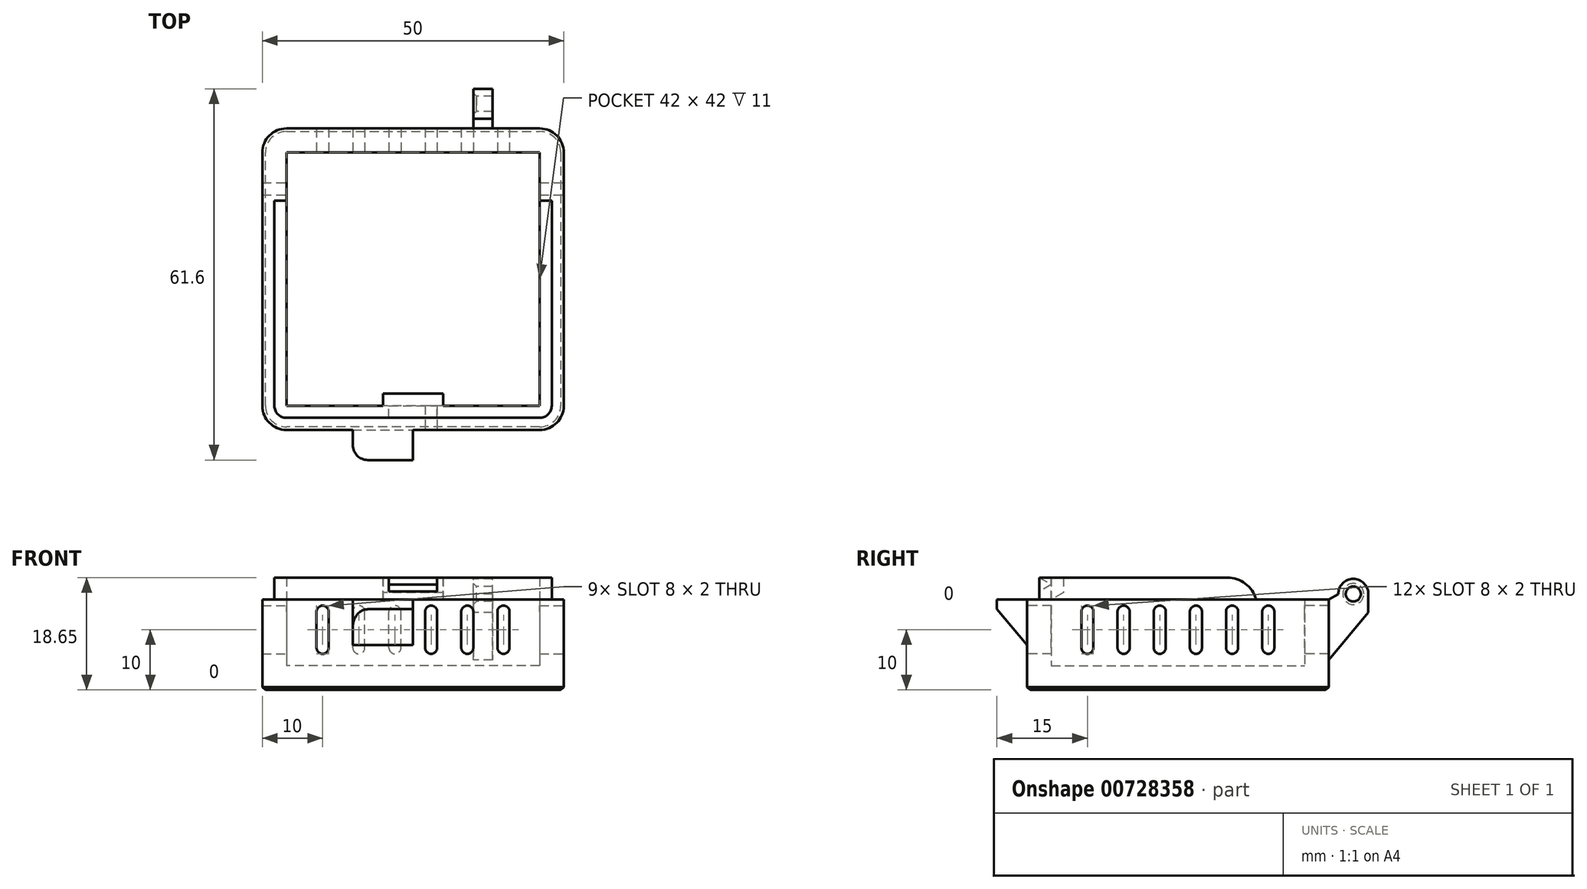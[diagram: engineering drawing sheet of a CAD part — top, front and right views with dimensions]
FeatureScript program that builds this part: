
annotation { "Feature Type Name" : "Feature", "Feature Type Description" : "" }
export const myFeature = defineFeature(function(context is Context, id is Id, definition is map)
    precondition{}
    {
        {
            var Q0;
            Q0=qCreatedBy(makeId("Top.planeOp"),FACE);
            var sketch = newSketch(context, id + "F0", { "sketchPlane" : qUnion([Q0])});
            skLineSegment(sketch, "E0.bottom", {"start": v(25, -25) * mm, "end": v(-25, -25) * mm});
            skLineSegment(sketch, "E0.top", {"start": v(25, 25) * mm, "end": v(-25, 25) * mm});
            skLineSegment(sketch, "E0.left", {"start": v(25, -25) * mm, "end": v(25, 25) * mm});
            skLineSegment(sketch, "E0.right", {"start": v(-25, -25) * mm, "end": v(-25, 25) * mm});
            skPoint(sketch, "E0.middle", {"position": v(0, 0) * mm});
            skSolve(sketch);
        }
        {
            var Q0;
            Q0=qSketchRegion(id+"F0",true);
            extrude(context, id + "F1", {"entities" : qUnion([Q0]), "depth" : 20 * mm, "offsetDistance" : 25 * mm});
        }
        {
            var Q0;
            Q0=makeQuery(id+"F1.opExtrude","CAP_FACE",FACE,{"disambiguationData":[OSD([sQuery(id+"F0.wireOp",EDGE,"E0.bottom"),sQuery(id+"F0.wireOp",EDGE,"E0.top"),sQuery(id+"F0.wireOp",EDGE,"E0.left"),sQuery(id+"F0.wireOp",EDGE,"E0.right")])],"isStart":false});
            shell(context, id + "F2", {"entities" : qUnion([Q0]), "thickness" : 4 * mm});
        }
        {
            var Q0;
            Q0=makeQuery(id+"F1.opExtrude","SWEPT_EDGE",EDGE,{"disambiguationData":[OSD([sQuery(id+"F0.wireOp",EDGE,"E0.bottom"),sQuery(id+"F0.wireOp",EDGE,"E0.right")])]});
            var Q1;
            Q1=makeQuery(id+"F1.opExtrude","SWEPT_EDGE",EDGE,{"disambiguationData":[OSD([sQuery(id+"F0.wireOp",EDGE,"E0.bottom"),sQuery(id+"F0.wireOp",EDGE,"E0.left")])]});
            var Q2;
            Q2=makeQuery(id+"F1.opExtrude","SWEPT_EDGE",EDGE,{"disambiguationData":[OSD([sQuery(id+"F0.wireOp",EDGE,"E0.top"),sQuery(id+"F0.wireOp",EDGE,"E0.left")])]});
            var Q3;
            Q3=makeQuery(id+"F1.opExtrude","SWEPT_EDGE",EDGE,{"disambiguationData":[OSD([sQuery(id+"F0.wireOp",EDGE,"E0.top"),sQuery(id+"F0.wireOp",EDGE,"E0.right")])]});
            fillet(context, id + "F3", {"entities" : qUnion([Q0, Q1, Q2, Q3]), "radius" : 4 * mm, "tangentPropagation" : true, "allowEdgeOverflow" : false});
        }
        {
            var Q0;
            Q0=makeQuery(id+"F1.opExtrude","SWEPT_FACE",FACE,{"disambiguationData":[OSD([sQuery(id+"F0.wireOp",EDGE,"E0.bottom")])]});
            var sketch = newSketch(context, id + "F4", { "sketchPlane" : qUnion([Q0])});
            skLineSegment(sketch, "E1.bottom", {"start": v(-15, 6) * mm, "end": v(-15, 6) * mm});
            skLineSegment(sketch, "E1.top", {"start": v(-15, 14) * mm, "end": v(-15, 14) * mm});
            skLineSegment(sketch, "E1.left", {"start": v(-14, 7) * mm, "end": v(-14, 13) * mm});
            skLineSegment(sketch, "E1.right", {"start": v(-16, 7) * mm, "end": v(-16, 13) * mm});
            skPoint(sketch, "E1.middle", {"position": v(-15, 10) * mm});
            skLineSegment(sketch, "E2.1.0.0", {"start": v(-9, 14) * mm, "end": v(-9, 14) * mm});
            skLineSegment(sketch, "E2.1.0.1", {"start": v(-10, 7) * mm, "end": v(-10, 13) * mm});
            skLineSegment(sketch, "E2.1.0.2", {"start": v(-9, 6) * mm, "end": v(-9, 6) * mm});
            skLineSegment(sketch, "E2.1.0.3", {"start": v(-8, 7) * mm, "end": v(-8, 13) * mm});
            skPoint(sketch, "E2.1.0.4", {"position": v(-9, 10) * mm});
            skLineSegment(sketch, "E2.2.0.0", {"start": v(-3, 14) * mm, "end": v(-3, 14) * mm});
            skLineSegment(sketch, "E2.2.0.1", {"start": v(-4, 7) * mm, "end": v(-4, 13) * mm});
            skLineSegment(sketch, "E2.2.0.2", {"start": v(-3, 6) * mm, "end": v(-3, 6) * mm});
            skLineSegment(sketch, "E2.2.0.3", {"start": v(-2, 7) * mm, "end": v(-2, 13) * mm});
            skPoint(sketch, "E2.2.0.4", {"position": v(-3, 10) * mm});
            skLineSegment(sketch, "E2.3.0.0", {"start": v(3, 14) * mm, "end": v(3, 14) * mm});
            skLineSegment(sketch, "E2.3.0.1", {"start": v(2, 7) * mm, "end": v(2, 13) * mm});
            skLineSegment(sketch, "E2.3.0.2", {"start": v(3, 6) * mm, "end": v(3, 6) * mm});
            skLineSegment(sketch, "E2.3.0.3", {"start": v(4, 7) * mm, "end": v(4, 13) * mm});
            skPoint(sketch, "E2.3.0.4", {"position": v(3, 10) * mm});
            skLineSegment(sketch, "E2.4.0.0", {"start": v(9, 14) * mm, "end": v(9, 14) * mm});
            skLineSegment(sketch, "E2.4.0.1", {"start": v(8, 7) * mm, "end": v(8, 13) * mm});
            skLineSegment(sketch, "E2.4.0.2", {"start": v(9, 6) * mm, "end": v(9, 6) * mm});
            skLineSegment(sketch, "E2.4.0.3", {"start": v(10, 7) * mm, "end": v(10, 13) * mm});
            skPoint(sketch, "E2.4.0.4", {"position": v(9, 10) * mm});
            skLineSegment(sketch, "E2.direction1", {"start": v(-16, 6) * mm, "end": v(-10, 6) * mm, "construction": true});
            skLineSegment(sketch, "E3.MirrorCS", {"start": v(15, 6) * mm, "end": v(15, 6) * mm});
            skLineSegment(sketch, "E4.MirrorCS", {"start": v(16, 7) * mm, "end": v(16, 13) * mm});
            skLineSegment(sketch, "E5.MirrorCS", {"start": v(14, 7) * mm, "end": v(14, 13) * mm});
            skLineSegment(sketch, "E6.MirrorCS", {"start": v(15, 14) * mm, "end": v(15, 14) * mm});
            skPoint(sketch, "E7.MirrorP", {"position": v(15, 10) * mm});
            skLineSegment(sketch, "E8.MirrorCS", {"start": v(16, 6) * mm, "end": v(10, 6) * mm, "construction": true});
            skPoint(sketch, "E9.visualSharp", {"position": v(-16, 14) * mm});
            skArc(sketch, "E9.filletArc", {"start": v(-15, 14) * mm, "mid": v(-15.7, 13.7) * mm, "end": v(-16, 13) * mm});
            skPoint(sketch, "E10.visualSharp", {"position": v(-14, 14) * mm});
            skArc(sketch, "E10.filletArc", {"start": v(-14, 13) * mm, "mid": v(-14.3, 13.7) * mm, "end": v(-15, 14) * mm});
            skPoint(sketch, "E11.visualSharp", {"position": v(-16, 6) * mm});
            skArc(sketch, "E11.filletArc", {"start": v(-16, 7) * mm, "mid": v(-15.7, 6.3) * mm, "end": v(-15, 6) * mm});
            skPoint(sketch, "E12.visualSharp", {"position": v(-14, 6) * mm});
            skArc(sketch, "E12.filletArc", {"start": v(-15, 6) * mm, "mid": v(-14.3, 6.3) * mm, "end": v(-14, 7) * mm});
            skPoint(sketch, "E13.visualSharp", {"position": v(-10, 14) * mm});
            skArc(sketch, "E13.filletArc", {"start": v(-9, 14) * mm, "mid": v(-9.7, 13.7) * mm, "end": v(-10, 13) * mm});
            skPoint(sketch, "E14.visualSharp", {"position": v(-8, 14) * mm});
            skArc(sketch, "E14.filletArc", {"start": v(-8, 13) * mm, "mid": v(-8.3, 13.7) * mm, "end": v(-9, 14) * mm});
            skPoint(sketch, "E15.visualSharp", {"position": v(-8, 6) * mm});
            skArc(sketch, "E15.filletArc", {"start": v(-9, 6) * mm, "mid": v(-8.3, 6.3) * mm, "end": v(-8, 7) * mm});
            skPoint(sketch, "E16.visualSharp", {"position": v(-10, 6) * mm});
            skArc(sketch, "E16.filletArc", {"start": v(-10, 7) * mm, "mid": v(-9.7, 6.3) * mm, "end": v(-9, 6) * mm});
            skPoint(sketch, "E17.visualSharp", {"position": v(-4, 6) * mm});
            skArc(sketch, "E17.filletArc", {"start": v(-4, 7) * mm, "mid": v(-3.7, 6.3) * mm, "end": v(-3, 6) * mm});
            skPoint(sketch, "E18.visualSharp", {"position": v(-2, 6) * mm});
            skArc(sketch, "E18.filletArc", {"start": v(-3, 6) * mm, "mid": v(-2.3, 6.3) * mm, "end": v(-2, 7) * mm});
            skPoint(sketch, "E19.visualSharp", {"position": v(-2, 14) * mm});
            skArc(sketch, "E19.filletArc", {"start": v(-2, 13) * mm, "mid": v(-2.3, 13.7) * mm, "end": v(-3, 14) * mm});
            skPoint(sketch, "E20.visualSharp", {"position": v(-4, 14) * mm});
            skArc(sketch, "E20.filletArc", {"start": v(-3, 14) * mm, "mid": v(-3.7, 13.7) * mm, "end": v(-4, 13) * mm});
            skPoint(sketch, "E21.visualSharp", {"position": v(2, 14) * mm});
            skArc(sketch, "E21.filletArc", {"start": v(3, 14) * mm, "mid": v(2.3, 13.7) * mm, "end": v(2, 13) * mm});
            skPoint(sketch, "E22.visualSharp", {"position": v(4, 14) * mm});
            skArc(sketch, "E22.filletArc", {"start": v(4, 13) * mm, "mid": v(3.7, 13.7) * mm, "end": v(3, 14) * mm});
            skPoint(sketch, "E23.visualSharp", {"position": v(4, 6) * mm});
            skArc(sketch, "E23.filletArc", {"start": v(3, 6) * mm, "mid": v(3.7, 6.3) * mm, "end": v(4, 7) * mm});
            skPoint(sketch, "E24.visualSharp", {"position": v(2, 6) * mm});
            skArc(sketch, "E24.filletArc", {"start": v(2, 7) * mm, "mid": v(2.3, 6.3) * mm, "end": v(3, 6) * mm});
            skPoint(sketch, "E25.visualSharp", {"position": v(10, 14) * mm});
            skArc(sketch, "E25.filletArc", {"start": v(10, 13) * mm, "mid": v(9.7, 13.7) * mm, "end": v(9, 14) * mm});
            skPoint(sketch, "E26.visualSharp", {"position": v(8, 14) * mm});
            skArc(sketch, "E26.filletArc", {"start": v(9, 14) * mm, "mid": v(8.3, 13.7) * mm, "end": v(8, 13) * mm});
            skPoint(sketch, "E27.visualSharp", {"position": v(8, 6) * mm});
            skArc(sketch, "E27.filletArc", {"start": v(8, 7) * mm, "mid": v(8.3, 6.3) * mm, "end": v(9, 6) * mm});
            skPoint(sketch, "E28.visualSharp", {"position": v(10, 6) * mm});
            skArc(sketch, "E28.filletArc", {"start": v(9, 6) * mm, "mid": v(9.7, 6.3) * mm, "end": v(10, 7) * mm});
            skPoint(sketch, "E29.visualSharp", {"position": v(16, 14) * mm});
            skArc(sketch, "E29.filletArc", {"start": v(16, 13) * mm, "mid": v(15.7, 13.7) * mm, "end": v(15, 14) * mm});
            skPoint(sketch, "E30.visualSharp", {"position": v(14, 14) * mm});
            skArc(sketch, "E30.filletArc", {"start": v(15, 14) * mm, "mid": v(14.3, 13.7) * mm, "end": v(14, 13) * mm});
            skPoint(sketch, "E31.visualSharp", {"position": v(16, 6) * mm});
            skArc(sketch, "E31.filletArc", {"start": v(15, 6) * mm, "mid": v(15.7, 6.3) * mm, "end": v(16, 7) * mm});
            skPoint(sketch, "E32.visualSharp", {"position": v(14, 6) * mm});
            skArc(sketch, "E32.filletArc", {"start": v(14, 7) * mm, "mid": v(14.3, 6.3) * mm, "end": v(15, 6) * mm});
            skSolve(sketch);
        }
        {
            var Q0;
            Q0=qSketchRegion(id+"F4",true);
            extrude(context, id + "F5", {"entities" : qUnion([Q0]), "operationType" : NewBodyOperationType.REMOVE, "oppositeDirection" : true, "depth" : 50 * mm, "offsetDistance" : 25 * mm});
        }
        {
            var Q0;
            Q0=makeQuery(id+"F1.opExtrude","SWEPT_FACE",FACE,{"disambiguationData":[OSD([sQuery(id+"F0.wireOp",EDGE,"E0.left")])]});
            var sketch = newSketch(context, id + "F6", { "sketchPlane" : qUnion([Q0])});
            skLineSegment(sketch, "E33.bottom", {"start": v(-15, 6) * mm, "end": v(-15, 6) * mm});
            skLineSegment(sketch, "E33.top", {"start": v(-15, 14) * mm, "end": v(-15, 14) * mm});
            skLineSegment(sketch, "E33.left", {"start": v(-14, 7) * mm, "end": v(-14, 13) * mm});
            skLineSegment(sketch, "E33.right", {"start": v(-16, 7) * mm, "end": v(-16, 13) * mm});
            skPoint(sketch, "E33.middle", {"position": v(-15, 10) * mm});
            skPoint(sketch, "E34.visualSharp", {"position": v(-16, 14) * mm});
            skArc(sketch, "E34.filletArc", {"start": v(-15, 14) * mm, "mid": v(-15.7, 13.7) * mm, "end": v(-16, 13) * mm});
            skPoint(sketch, "E35.visualSharp", {"position": v(-14, 14) * mm});
            skArc(sketch, "E35.filletArc", {"start": v(-14, 13) * mm, "mid": v(-14.3, 13.7) * mm, "end": v(-15, 14) * mm});
            skPoint(sketch, "E36.visualSharp", {"position": v(-14, 6) * mm});
            skArc(sketch, "E36.filletArc", {"start": v(-15, 6) * mm, "mid": v(-14.3, 6.3) * mm, "end": v(-14, 7) * mm});
            skPoint(sketch, "E37.visualSharp", {"position": v(-16, 6) * mm});
            skArc(sketch, "E37.filletArc", {"start": v(-16, 7) * mm, "mid": v(-15.7, 6.3) * mm, "end": v(-15, 6) * mm});
            skPoint(sketch, "E38.1.0.0", {"position": v(-8, 6) * mm});
            skPoint(sketch, "E38.1.0.1", {"position": v(-10, 6) * mm});
            skLineSegment(sketch, "E38.1.0.2", {"start": v(-10, 7) * mm, "end": v(-10, 13) * mm});
            skLineSegment(sketch, "E38.1.0.3", {"start": v(-8, 7) * mm, "end": v(-8, 13) * mm});
            skPoint(sketch, "E38.1.0.4", {"position": v(-8, 14) * mm});
            skPoint(sketch, "E38.1.0.5", {"position": v(-10, 14) * mm});
            skPoint(sketch, "E38.1.0.6", {"position": v(-9, 10) * mm});
            skArc(sketch, "E38.1.0.7", {"start": v(-9, 6) * mm, "mid": v(-8.3, 6.3) * mm, "end": v(-8, 7) * mm});
            skArc(sketch, "E38.1.0.8", {"start": v(-8, 13) * mm, "mid": v(-8.3, 13.7) * mm, "end": v(-9, 14) * mm});
            skArc(sketch, "E38.1.0.9", {"start": v(-9, 14) * mm, "mid": v(-9.7, 13.7) * mm, "end": v(-10, 13) * mm});
            skArc(sketch, "E38.1.0.10", {"start": v(-10, 7) * mm, "mid": v(-9.7, 6.3) * mm, "end": v(-9, 6) * mm});
            skPoint(sketch, "E38.2.0.0", {"position": v(-2, 6) * mm});
            skPoint(sketch, "E38.2.0.1", {"position": v(-4, 6) * mm});
            skLineSegment(sketch, "E38.2.0.2", {"start": v(-4, 7) * mm, "end": v(-4, 13) * mm});
            skLineSegment(sketch, "E38.2.0.3", {"start": v(-2, 7) * mm, "end": v(-2, 13) * mm});
            skPoint(sketch, "E38.2.0.4", {"position": v(-2, 14) * mm});
            skPoint(sketch, "E38.2.0.5", {"position": v(-4, 14) * mm});
            skPoint(sketch, "E38.2.0.6", {"position": v(-3, 10) * mm});
            skArc(sketch, "E38.2.0.7", {"start": v(-3, 6) * mm, "mid": v(-2.3, 6.3) * mm, "end": v(-2, 7) * mm});
            skArc(sketch, "E38.2.0.8", {"start": v(-2, 13) * mm, "mid": v(-2.3, 13.7) * mm, "end": v(-3, 14) * mm});
            skArc(sketch, "E38.2.0.9", {"start": v(-3, 14) * mm, "mid": v(-3.7, 13.7) * mm, "end": v(-4, 13) * mm});
            skArc(sketch, "E38.2.0.10", {"start": v(-4, 7) * mm, "mid": v(-3.7, 6.3) * mm, "end": v(-3, 6) * mm});
            skLineSegment(sketch, "E38.direction1", {"start": v(-16, 6) * mm, "end": v(-10, 6) * mm, "construction": true});
            skArc(sketch, "E39.MirrorCS", {"start": v(10, 7) * mm, "mid": v(9.7, 6.3) * mm, "end": v(9, 6) * mm});
            skArc(sketch, "E40.MirrorCS", {"start": v(9, 14) * mm, "mid": v(9.7, 13.7) * mm, "end": v(10, 13) * mm});
            skArc(sketch, "E41.MirrorCS", {"start": v(9, 6) * mm, "mid": v(8.3, 6.3) * mm, "end": v(8, 7) * mm});
            skArc(sketch, "E42.MirrorCS", {"start": v(16, 7) * mm, "mid": v(15.7, 6.3) * mm, "end": v(15, 6) * mm});
            skArc(sketch, "E43.MirrorCS", {"start": v(15, 6) * mm, "mid": v(14.3, 6.3) * mm, "end": v(14, 7) * mm});
            skArc(sketch, "E44.MirrorCS", {"start": v(14, 13) * mm, "mid": v(14.3, 13.7) * mm, "end": v(15, 14) * mm});
            skArc(sketch, "E45.MirrorCS", {"start": v(2, 13) * mm, "mid": v(2.3, 13.7) * mm, "end": v(3, 14) * mm});
            skArc(sketch, "E46.MirrorCS", {"start": v(3, 6) * mm, "mid": v(2.3, 6.3) * mm, "end": v(2, 7) * mm});
            skArc(sketch, "E47.MirrorCS", {"start": v(4, 7) * mm, "mid": v(3.7, 6.3) * mm, "end": v(3, 6) * mm});
            skArc(sketch, "E48.MirrorCS", {"start": v(8, 13) * mm, "mid": v(8.3, 13.7) * mm, "end": v(9, 14) * mm});
            skArc(sketch, "E49.MirrorCS", {"start": v(15, 14) * mm, "mid": v(15.7, 13.7) * mm, "end": v(16, 13) * mm});
            skArc(sketch, "E50.MirrorCS", {"start": v(3, 14) * mm, "mid": v(3.7, 13.7) * mm, "end": v(4, 13) * mm});
            skPoint(sketch, "E51.MirrorP", {"position": v(9, 10) * mm});
            skLineSegment(sketch, "E52.MirrorCS", {"start": v(4, 7) * mm, "end": v(4, 13) * mm});
            skLineSegment(sketch, "E53.MirrorCS", {"start": v(16, 6) * mm, "end": v(10, 6) * mm, "construction": true});
            skPoint(sketch, "E54.MirrorP", {"position": v(14, 14) * mm});
            skLineSegment(sketch, "E55.MirrorCS", {"start": v(8, 7) * mm, "end": v(8, 13) * mm});
            skPoint(sketch, "E56.MirrorP", {"position": v(4, 6) * mm});
            skPoint(sketch, "E57.MirrorP", {"position": v(14, 6) * mm});
            skPoint(sketch, "E58.MirrorP", {"position": v(4, 14) * mm});
            skLineSegment(sketch, "E59.MirrorCS", {"start": v(10, 7) * mm, "end": v(10, 13) * mm});
            skPoint(sketch, "E60.MirrorP", {"position": v(10, 6) * mm});
            skLineSegment(sketch, "E61.MirrorCS", {"start": v(15, 14) * mm, "end": v(15, 14) * mm});
            skLineSegment(sketch, "E62.MirrorCS", {"start": v(16, 7) * mm, "end": v(16, 13) * mm});
            skLineSegment(sketch, "E63.MirrorCS", {"start": v(14, 7) * mm, "end": v(14, 13) * mm});
            skLineSegment(sketch, "E64.MirrorCS", {"start": v(2, 7) * mm, "end": v(2, 13) * mm});
            skPoint(sketch, "E65.MirrorP", {"position": v(16, 14) * mm});
            skPoint(sketch, "E66.MirrorP", {"position": v(8, 14) * mm});
            skPoint(sketch, "E67.MirrorP", {"position": v(16, 6) * mm});
            skPoint(sketch, "E68.MirrorP", {"position": v(2, 14) * mm});
            skPoint(sketch, "E69.MirrorP", {"position": v(2, 6) * mm});
            skPoint(sketch, "E70.MirrorP", {"position": v(3, 10) * mm});
            skLineSegment(sketch, "E71.MirrorCS", {"start": v(15, 6) * mm, "end": v(15, 6) * mm});
            skPoint(sketch, "E72.MirrorP", {"position": v(15, 10) * mm});
            skPoint(sketch, "E73.MirrorP", {"position": v(8, 6) * mm});
            skPoint(sketch, "E74.MirrorP", {"position": v(10, 14) * mm});
            skSolve(sketch);
        }
        {
            var Q0;
            Q0=qSketchRegion(id+"F6",true);
            extrude(context, id + "F7", {"entities" : qUnion([Q0]), "operationType" : NewBodyOperationType.REMOVE, "endBound" : BoundingType.THROUGH_ALL, "oppositeDirection" : true, "depth" : 25 * mm, "offsetDistance" : 25 * mm});
        }
        {
            var Q0;
            Q0=makeQuery(id+"F1.opExtrude","CAP_FACE",FACE,{"disambiguationData":[OSD([sQuery(id+"F0.wireOp",EDGE,"E0.bottom"),sQuery(id+"F0.wireOp",EDGE,"E0.top"),sQuery(id+"F0.wireOp",EDGE,"E0.left"),sQuery(id+"F0.wireOp",EDGE,"E0.right")])],"isStart":false});
            var sketch = newSketch(context, id + "F8", { "sketchPlane" : qUnion([Q0])});
            skLineSegment(sketch, "E75.bottom", {"start": v(25, 25) * mm, "end": v(-25, 25) * mm});
            skLineSegment(sketch, "E75.top", {"start": v(25, -25) * mm, "end": v(-25, -25) * mm});
            skLineSegment(sketch, "E75.left", {"start": v(25, 25) * mm, "end": v(25, -25) * mm});
            skLineSegment(sketch, "E75.right", {"start": v(-25, 25) * mm, "end": v(-25, -25) * mm});
            skPoint(sketch, "E75.middle", {"position": v(0, 0) * mm});
            skLineSegment(sketch, "E76.bottom", {"start": v(23, 23) * mm, "end": v(-23, 23) * mm});
            skLineSegment(sketch, "E76.top", {"start": v(23, -23) * mm, "end": v(-23, -23) * mm});
            skLineSegment(sketch, "E76.left", {"start": v(23, 23) * mm, "end": v(23, -23) * mm});
            skLineSegment(sketch, "E76.right", {"start": v(-23, 23) * mm, "end": v(-23, -23) * mm});
            skSolve(sketch);
        }
        {
            var Q0;
            Q0=qSketchRegion(id+"F8",true);
            extrude(context, id + "F9", {"entities" : qUnion([Q0]), "operationType" : NewBodyOperationType.REMOVE, "oppositeDirection" : true, "depth" : 5 * mm, "offsetDistance" : 25 * mm});
        }
        {
            var Q0;
            Q0=makeQuery(id+"F9.boolean.opBoolean","COPY",EDGE,{"derivedFrom":makeQuery(id+"F9.opExtrude","SWEPT_EDGE",EDGE,{"disambiguationData":[OSD([sQuery(id+"F8.wireOp",EDGE,"E76.bottom"),sQuery(id+"F8.wireOp",EDGE,"E76.right")])]})});
            var Q1;
            Q1=makeQuery(id+"F9.boolean.opBoolean","COPY",EDGE,{"derivedFrom":makeQuery(id+"F9.opExtrude","SWEPT_EDGE",EDGE,{"disambiguationData":[OSD([sQuery(id+"F8.wireOp",EDGE,"E76.top"),sQuery(id+"F8.wireOp",EDGE,"E76.right")])]})});
            var Q2;
            Q2=makeQuery(id+"F9.boolean.opBoolean","COPY",EDGE,{"derivedFrom":makeQuery(id+"F9.opExtrude","SWEPT_EDGE",EDGE,{"disambiguationData":[OSD([sQuery(id+"F8.wireOp",EDGE,"E76.top"),sQuery(id+"F8.wireOp",EDGE,"E76.left")])]})});
            fillet(context, id + "F10", {"entities" : qUnion([Q0, Q1, Q2]), "radius" : 2 * mm, "tangentPropagation" : true, "allowEdgeOverflow" : false});
        }
        {
            var Q0;
            Q0=qCreatedBy(makeId("Right.planeOp"),FACE);
            var sketch = newSketch(context, id + "F11", { "sketchPlane" : qUnion([Q0])});
            skLineSegment(sketch, "E77", {"start": v(21, 20) * mm, "end": v(19, 18.85) * mm, "construction": true});
            skLineSegment(sketch, "E78", {"start": v(19, 18.85) * mm, "end": v(19, 16.15) * mm, "construction": true});
            skLineSegment(sketch, "E79", {"start": v(19, 16.15) * mm, "end": v(21, 15) * mm, "construction": true});
            skLineSegment(sketch, "E80", {"start": v(21, 15) * mm, "end": v(21, 20) * mm, "construction": true});
            skLineSegment(sketch, "E81.MirrorCS", {"start": v(-21, 20) * mm, "end": v(-19, 18.85) * mm});
            skLineSegment(sketch, "E82.MirrorCS", {"start": v(-19, 18.85) * mm, "end": v(-19, 16.15) * mm});
            skLineSegment(sketch, "E83.MirrorCS", {"start": v(-21, 15) * mm, "end": v(-21, 20) * mm});
            skLineSegment(sketch, "E84.MirrorCS", {"start": v(-19, 16.15) * mm, "end": v(-21, 15) * mm});
            skSolve(sketch);
        }
        {
            var Q0;
            Q0=qSketchRegion(id+"F11",true);
            extrude(context, id + "F12", {"entities" : qUnion([Q0]), "operationType" : NewBodyOperationType.ADD, "endBound" : BoundingType.SYMMETRIC, "depth" : 10 * mm, "offsetDistance" : 25 * mm});
        }
        {
            var Q0;
            Q0=qCreatedBy(makeId("Right.planeOp"),FACE);
            var sketch = newSketch(context, id + "F13", { "sketchPlane" : qUnion([Q0])});
            skLineSegment(sketch, "E85", {"start": v(23, 18.65) * mm, "end": v(21, 17.5) * mm, "construction": true});
            skLineSegment(sketch, "E86", {"start": v(21, 17.5) * mm, "end": v(23, 16.35) * mm, "construction": true});
            skLineSegment(sketch, "E87", {"start": v(23, 16.35) * mm, "end": v(23, 18.65) * mm, "construction": true});
            skLineSegment(sketch, "E88.MirrorCS", {"start": v(-23, 18.65) * mm, "end": v(-21, 17.5) * mm});
            skLineSegment(sketch, "E89.MirrorCS", {"start": v(-21, 17.5) * mm, "end": v(-23, 16.35) * mm});
            skLineSegment(sketch, "E90.MirrorCS", {"start": v(-23, 16.35) * mm, "end": v(-23, 18.65) * mm});
            skSolve(sketch);
        }
        {
            var Q0;
            Q0=qSketchRegion(id+"F13",true);
            extrude(context, id + "F14", {"entities" : qUnion([Q0]), "operationType" : NewBodyOperationType.REMOVE, "endBound" : BoundingType.SYMMETRIC, "oppositeDirection" : true, "depth" : 8 * mm, "offsetDistance" : 25 * mm});
        }
        {
            var Q0;
            Q0=makeQuery(id+"F1.opExtrude","CAP_FACE",FACE,{"disambiguationData":[OSD([sQuery(id+"F0.wireOp",EDGE,"E0.bottom"),sQuery(id+"F0.wireOp",EDGE,"E0.top"),sQuery(id+"F0.wireOp",EDGE,"E0.left"),sQuery(id+"F0.wireOp",EDGE,"E0.right")])],"isStart":false});
            var sketch = newSketch(context, id + "F15", { "sketchPlane" : qUnion([Q0])});
            skLineSegment(sketch, "E91.bottom", {"start": v(23, -23) * mm, "end": v(-23, -23) * mm});
            skLineSegment(sketch, "E91.top", {"start": v(23, 23) * mm, "end": v(-23, 23) * mm});
            skLineSegment(sketch, "E91.left", {"start": v(23, -23) * mm, "end": v(23, 23) * mm});
            skLineSegment(sketch, "E91.right", {"start": v(-23, -23) * mm, "end": v(-23, 23) * mm});
            skPoint(sketch, "E91.middle", {"position": v(0, 0) * mm});
            skSolve(sketch);
        }
        {
            var Q0;
            Q0=qSketchRegion(id+"F15",true);
            extrude(context, id + "F16", {"entities" : qUnion([Q0]), "operationType" : NewBodyOperationType.REMOVE, "oppositeDirection" : true, "depth" : 1.35 * mm, "offsetDistance" : 25 * mm});
        }
        {
            var Q0;
            Q0=makeQuery(id+"F9.boolean.opBoolean","COPY",FACE,{"derivedFrom":makeQuery(id+"F9.opExtrude","CAP_FACE",FACE,{"disambiguationData":[OSD([sQuery(id+"F8.wireOp",EDGE,"E75.bottom"),sQuery(id+"F8.wireOp",EDGE,"E75.top"),sQuery(id+"F8.wireOp",EDGE,"E75.left"),sQuery(id+"F8.wireOp",EDGE,"E75.right"),sQuery(id+"F8.wireOp",EDGE,"E76.bottom"),sQuery(id+"F8.wireOp",EDGE,"E76.top"),sQuery(id+"F8.wireOp",EDGE,"E76.left"),sQuery(id+"F8.wireOp",EDGE,"E76.right")])],"isStart":false})});
            var sketch = newSketch(context, id + "F17", { "sketchPlane" : qUnion([Q0])});
            skLineSegment(sketch, "E92.bottom", {"start": v(23, 23) * mm, "end": v(-23, 23) * mm});
            skLineSegment(sketch, "E92.top", {"start": v(23, 13) * mm, "end": v(-23, 13) * mm});
            skLineSegment(sketch, "E92.left", {"start": v(23, 23) * mm, "end": v(23, 13) * mm});
            skLineSegment(sketch, "E92.right", {"start": v(-23, 23) * mm, "end": v(-23, 13) * mm});
            skPoint(sketch, "E92.middle", {"position": v(0, 18) * mm});
            skSolve(sketch);
        }
        {
            var Q0;
            Q0=qSketchRegion(id+"F17",true);
            extrude(context, id + "F18", {"entities" : qUnion([Q0]), "operationType" : NewBodyOperationType.REMOVE, "depth" : 25 * mm, "offsetDistance" : 25 * mm});
        }
        {
            var Q0;
            Q0=makeQuery(id+"F18.boolean.opBoolean","INTERSECT",EDGE,{"disambiguationData":[OD(1.0)],"derivedFrom":[makeQuery(id+"F16.boolean.opBoolean","COPY",FACE,{"derivedFrom":makeQuery(id+"F16.opExtrude","CAP_FACE",FACE,{"disambiguationData":[OSD([sQuery(id+"F15.wireOp",EDGE,"E91.bottom"),sQuery(id+"F15.wireOp",EDGE,"E91.top"),sQuery(id+"F15.wireOp",EDGE,"E91.left"),sQuery(id+"F15.wireOp",EDGE,"E91.right")])],"isStart":false})}),makeQuery(id+"F18.opExtrude","SWEPT_FACE",FACE,{"disambiguationData":[OSD([sQuery(id+"F17.wireOp",EDGE,"E92.top")])]})]});
            var Q1;
            Q1=makeQuery(id+"F18.boolean.opBoolean","INTERSECT",EDGE,{"disambiguationData":[OD(0.0)],"derivedFrom":[makeQuery(id+"F16.boolean.opBoolean","COPY",FACE,{"derivedFrom":makeQuery(id+"F16.opExtrude","CAP_FACE",FACE,{"disambiguationData":[OSD([sQuery(id+"F15.wireOp",EDGE,"E91.bottom"),sQuery(id+"F15.wireOp",EDGE,"E91.top"),sQuery(id+"F15.wireOp",EDGE,"E91.left"),sQuery(id+"F15.wireOp",EDGE,"E91.right")])],"isStart":false})}),makeQuery(id+"F18.opExtrude","SWEPT_FACE",FACE,{"disambiguationData":[OSD([sQuery(id+"F17.wireOp",EDGE,"E92.top")])]})]});
            fillet(context, id + "F19", {"entities" : qUnion([Q0, Q1]), "radius" : 5 * mm, "tangentPropagation" : true, "allowEdgeOverflow" : false});
        }
        {
            var Q0;
            Q0=qCreatedBy(makeId("Right.planeOp"),FACE);
            cPlane(context, id + "F20", {"entities" : qUnion([Q0]), "cplaneType" : CPlaneType.OFFSET, "offset" : 10 * mm, "width" : 150 * mm, "height" : 150 * mm});
        }
        {
            var Q0;
            Q0=qCreatedBy(id+"F20.planeOp",FACE);
            var sketch = newSketch(context, id + "F21", { "sketchPlane" : qUnion([Q0])});
            skLineSegment(sketch, "E93", {"start": v(25, 15) * mm, "end": v(25, 5) * mm});
            skLineSegment(sketch, "E94", {"start": v(25, 5) * mm, "end": v(31.6, 12.87) * mm});
            skLineSegment(sketch, "E95", {"start": v(31.6, 12.87) * mm, "end": v(31.6, 18.42) * mm});
            skLineSegment(sketch, "E96", {"start": v(31.6, 18.42) * mm, "end": v(26.6, 18.42) * mm});
            skLineSegment(sketch, "E97", {"start": v(26.6, 18.42) * mm, "end": v(26.6, 15.92) * mm});
            skLineSegment(sketch, "E98", {"start": v(26.6, 15.92) * mm, "end": v(25, 15) * mm});
            skCircle(sketch, "E99", {"center": v(29.1, 15.92) * mm, "radius": 1.25 * mm});
            skSolve(sketch);
        }
        {
            var Q0;
            Q0=qSketchRegion(id+"F21",true);
            extrude(context, id + "F22", {"entities" : qUnion([Q0]), "operationType" : NewBodyOperationType.ADD, "depth" : 3.2 * mm, "offsetDistance" : 25 * mm});
        }
        {
            var Q0;
            Q0=makeQuery(id+"F22.opExtrude","SWEPT_EDGE",EDGE,{"disambiguationData":[OSD([sQuery(id+"F21.wireOp",EDGE,"E96"),sQuery(id+"F21.wireOp",EDGE,"E97")])]});
            var Q1;
            Q1=makeQuery(id+"F22.opExtrude","SWEPT_EDGE",EDGE,{"disambiguationData":[OSD([sQuery(id+"F21.wireOp",EDGE,"E95"),sQuery(id+"F21.wireOp",EDGE,"E96")])]});
            fillet(context, id + "F23", {"entities" : qUnion([Q0, Q1]), "radius" : 2.5 * mm, "tangentPropagation" : true, "allowEdgeOverflow" : false});
        }
        {
            var Q0;
            Q0=makeQuery(id+"F1.opExtrude","SWEPT_FACE",FACE,{"disambiguationData":[OSD([sQuery(id+"F0.wireOp",EDGE,"E0.bottom")])]});
            var sketch = newSketch(context, id + "F24", { "sketchPlane" : qUnion([Q0])});
            skLineSegment(sketch, "E100.bottom", {"start": v(0, 15) * mm, "end": v(-12, 15) * mm});
            skLineSegment(sketch, "E100.top", {"start": v(0, 0) * mm, "end": v(-12, 0) * mm});
            skLineSegment(sketch, "E100.left", {"start": v(0, 15) * mm, "end": v(0, 0) * mm});
            skLineSegment(sketch, "E100.right", {"start": v(-12, 15) * mm, "end": v(-12, 0) * mm});
            skPoint(sketch, "E100.middle", {"position": v(-6, 7.5) * mm});
            skSolve(sketch);
        }
        {
            var Q0;
            Q0=qSketchRegion(id+"F24",true);
            extrude(context, id + "F25", {"entities" : qUnion([Q0]), "operationType" : NewBodyOperationType.ADD, "oppositeDirection" : true, "depth" : 4 * mm, "offsetDistance" : 25 * mm});
        }
        {
            var Q0;
            Q0=qCreatedBy(makeId("Right.planeOp"),FACE);
            var sketch = newSketch(context, id + "F26", { "sketchPlane" : qUnion([Q0])});
            skLineSegment(sketch, "E101", {"start": v(-25, 15) * mm, "end": v(-25, 7.44) * mm});
            skLineSegment(sketch, "E102", {"start": v(-25, 7.44) * mm, "end": v(-30, 13.4) * mm});
            skLineSegment(sketch, "E103", {"start": v(-30, 13.4) * mm, "end": v(-30, 15) * mm});
            skLineSegment(sketch, "E104", {"start": v(-30, 15) * mm, "end": v(-25, 15) * mm});
            skSolve(sketch);
        }
        {
            var Q0;
            Q0=qSketchRegion(id+"F26",true);
            extrude(context, id + "F27", {"entities" : qUnion([Q0]), "operationType" : NewBodyOperationType.ADD, "oppositeDirection" : true, "depth" : 10 * mm, "offsetDistance" : 25 * mm});
        }
        {
            var Q0;
            Q0=makeQuery(id+"F22.opExtrude","CAP_EDGE",EDGE,{"disambiguationData":[OSD([sQuery(id+"F21.wireOp",EDGE,"E99")])],"isStart":true});
            var Q1;
            Q1=makeQuery(id+"FqFombIubLjZ8dA_1.1.F22.opExtrude","CAP_EDGE",EDGE,{"disambiguationData":[OSD([sQuery(id+"F21.wireOp",EDGE,"E99")])],"isStart":true});
            chamfer(context, id + "F28", {"entities" : qUnion([Q0, Q1]), "width" : .5 * mm, "tangentPropagation" : true});
        }
        {
            var Q0;
            Q0=makeQuery(id+"F1.opExtrude","CAP_EDGE",EDGE,{"disambiguationData":[OSD([sQuery(id+"F0.wireOp",EDGE,"E0.left")])],"isStart":true});
            chamfer(context, id + "F29", {"entities" : qUnion([Q0]), "width" : .5 * mm, "tangentPropagation" : true});
        }
        {
            var Q0;
            Q0=makeQuery(id+"F27.opExtrude","CAP_EDGE",EDGE,{"disambiguationData":[OSD([sQuery(id+"F26.wireOp",EDGE,"E103")])],"isStart":false});
            fillet(context, id + "F30", {"entities" : qUnion([Q0]), "radius" : 2.5 * mm, "tangentPropagation" : true, "allowEdgeOverflow" : false});
        }
    });
